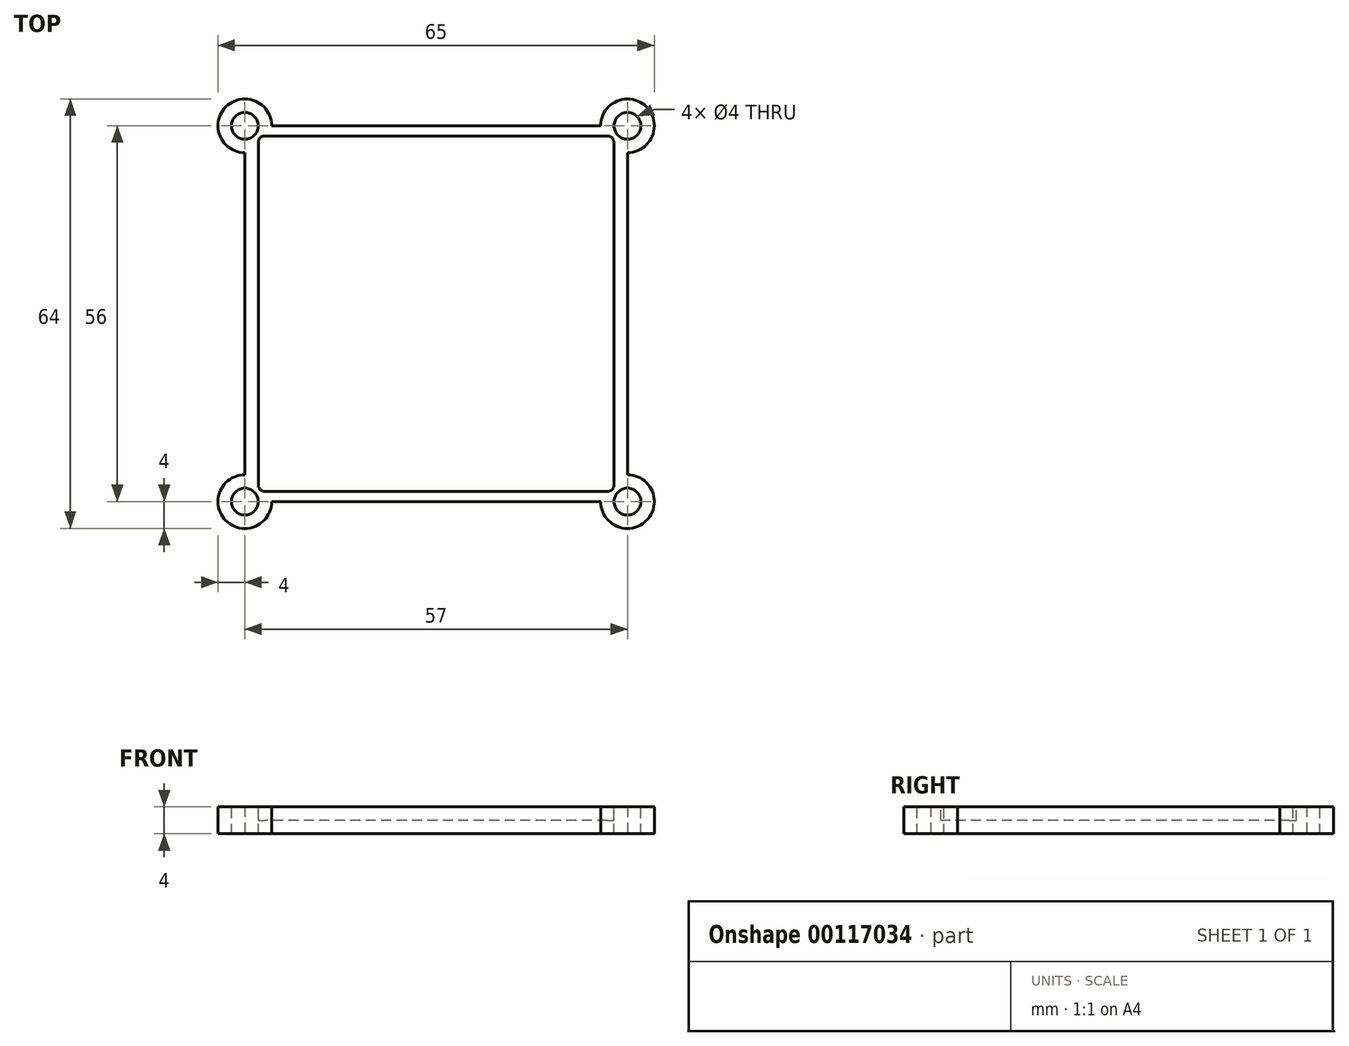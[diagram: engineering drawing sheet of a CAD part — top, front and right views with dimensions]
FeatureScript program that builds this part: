
annotation { "Feature Type Name" : "Feature", "Feature Type Description" : "" }
export const myFeature = defineFeature(function(context is Context, id is Id, definition is map)
    precondition{}
    {
        {
            var Q0;
            Q0=qCreatedBy(makeId("Top.planeOp"),FACE);
            var sketch = newSketch(context, id + "F0", { "sketchPlane" : qUnion([Q0])});
            skLineSegment(sketch, "E0.bottom", {"start": v(26.25, -26.25) * mm, "end": v(-26.25, -26.25) * mm, "construction": true});
            skLineSegment(sketch, "E0.top", {"start": v(26.25, 26.25) * mm, "end": v(-26.25, 26.25) * mm, "construction": true});
            skLineSegment(sketch, "E0.left", {"start": v(26.25, -26.25) * mm, "end": v(26.25, 26.25) * mm, "construction": true});
            skLineSegment(sketch, "E0.right", {"start": v(-26.25, -26.25) * mm, "end": v(-26.25, 26.25) * mm, "construction": true});
            skPoint(sketch, "E0.middle", {"position": v(0, 0) * mm});
            skLineSegment(sketch, "E1.bottom", {"start": v(28.5, 28) * mm, "end": v(-28.5, 28) * mm});
            skLineSegment(sketch, "E1.top", {"start": v(28.5, -28) * mm, "end": v(-28.5, -28) * mm});
            skLineSegment(sketch, "E1.left", {"start": v(28.5, 28) * mm, "end": v(28.5, -28) * mm});
            skLineSegment(sketch, "E1.right", {"start": v(-28.5, 28) * mm, "end": v(-28.5, -28) * mm});
            skCircle(sketch, "E2", {"center": v(28.5, -28) * mm, "radius": 4 * mm});
            skCircle(sketch, "E3", {"center": v(28.5, 28) * mm, "radius": 4 * mm});
            skCircle(sketch, "E4", {"center": v(-28.5, 28) * mm, "radius": 4 * mm});
            skCircle(sketch, "E5", {"center": v(-28.5, -28) * mm, "radius": 4 * mm});
            skSolve(sketch);
        }
        {
            var Q0;
            Q0 = qSketchRegion(id + "F0", true);
            extrude(context, id + "F1", {"entities" : qUnion([Q0]), "depth" : 4 * mm});
        }
        {
            var Q0;
            Q0=makeQuery(id+"F1.opExtrude","CAP_FACE",FACE,{"disambiguationData":[OSD([sQuery(id+"F0.wireOp",EDGE,"E1.bottom"),sQuery(id+"F0.wireOp",EDGE,"E1.top"),sQuery(id+"F0.wireOp",EDGE,"E1.left"),sQuery(id+"F0.wireOp",EDGE,"E1.right"),sQuery(id+"F0.wireOp",EDGE,"E2"),sQuery(id+"F0.wireOp",EDGE,"E3"),sQuery(id+"F0.wireOp",EDGE,"E4"),sQuery(id+"F0.wireOp",EDGE,"E5")])],"isStart":false});
            var sketch = newSketch(context, id + "F2", { "sketchPlane" : qUnion([Q0])});
            skCircle(sketch, "E6", {"center": v(-28.5, 28) * mm, "radius": 2 * mm});
            skCircle(sketch, "E7", {"center": v(28.5, 28) * mm, "radius": 2 * mm});
            skCircle(sketch, "E8", {"center": v(28.5, -28) * mm, "radius": 2 * mm});
            skCircle(sketch, "E9", {"center": v(-28.5, -28) * mm, "radius": 2 * mm});
            skSolve(sketch);
        }
        {
            var Q0;
            Q0 = qSketchRegion(id + "F2", true);
            extrude(context, id + "F3", {"entities" : qUnion([Q0]), "operationType" : NewBodyOperationType.REMOVE, "endBound" : BoundingType.UP_TO_NEXT, "oppositeDirection" : true, "depth" : 25 * mm});
        }
        {
            var Q0;
            Q0=makeQuery(id+"F1.opExtrude","CAP_FACE",FACE,{"disambiguationData":[OSD([sQuery(id+"F0.wireOp",EDGE,"E1.bottom"),sQuery(id+"F0.wireOp",EDGE,"E1.top"),sQuery(id+"F0.wireOp",EDGE,"E1.left"),sQuery(id+"F0.wireOp",EDGE,"E1.right"),sQuery(id+"F0.wireOp",EDGE,"E2"),sQuery(id+"F0.wireOp",EDGE,"E3"),sQuery(id+"F0.wireOp",EDGE,"E4"),sQuery(id+"F0.wireOp",EDGE,"E5")])],"isStart":false});
            var sketch = newSketch(context, id + "F4", { "sketchPlane" : qUnion([Q0])});
            skLineSegment(sketch, "E10.bottom", {"start": v(26.5, 26.5) * mm, "end": v(-26.5, 26.5) * mm});
            skLineSegment(sketch, "E10.top", {"start": v(26.5, -26.5) * mm, "end": v(-26.5, -26.5) * mm});
            skLineSegment(sketch, "E10.left", {"start": v(26.5, 26.5) * mm, "end": v(26.5, -26.5) * mm});
            skLineSegment(sketch, "E10.right", {"start": v(-26.5, 26.5) * mm, "end": v(-26.5, -26.5) * mm});
            skPoint(sketch, "E10.middle", {"position": v(0, 0) * mm});
            skSolve(sketch);
        }
        {
            var Q0;
            Q0 = qSketchRegion(id + "F4", true);
            extrude(context, id + "F5", {"entities" : qUnion([Q0]), "operationType" : NewBodyOperationType.REMOVE, "oppositeDirection" : true, "depth" : 2 * mm});
        }
        {
            var Q0;
            Q0=makeQuery(id+"F5.boolean.opBoolean","COPY",EDGE,{"derivedFrom":makeQuery(id+"F5.opExtrude","SWEPT_EDGE",EDGE,{"disambiguationData":[OSD([sQuery(id+"F4.wireOp",EDGE,"E10.bottom"),sQuery(id+"F4.wireOp",EDGE,"E10.right")])]})});
            var Q1;
            Q1=makeQuery(id+"F5.boolean.opBoolean","COPY",EDGE,{"derivedFrom":makeQuery(id+"F5.opExtrude","SWEPT_EDGE",EDGE,{"disambiguationData":[OSD([sQuery(id+"F4.wireOp",EDGE,"E10.bottom"),sQuery(id+"F4.wireOp",EDGE,"E10.left")])]})});
            var Q2;
            Q2=makeQuery(id+"F5.boolean.opBoolean","COPY",EDGE,{"derivedFrom":makeQuery(id+"F5.opExtrude","SWEPT_EDGE",EDGE,{"disambiguationData":[OSD([sQuery(id+"F4.wireOp",EDGE,"E10.top"),sQuery(id+"F4.wireOp",EDGE,"E10.left")])]})});
            var Q3;
            Q3=makeQuery(id+"F5.boolean.opBoolean","COPY",EDGE,{"derivedFrom":makeQuery(id+"F5.opExtrude","SWEPT_EDGE",EDGE,{"disambiguationData":[OSD([sQuery(id+"F4.wireOp",EDGE,"E10.top"),sQuery(id+"F4.wireOp",EDGE,"E10.right")])]})});
            fillet(context, id + "F6", {"entities" : qUnion([Q0, Q1, Q2, Q3]), "radius" : 1 * mm, "tangentPropagation" : true, "allowEdgeOverflow" : false});
        }
    });
